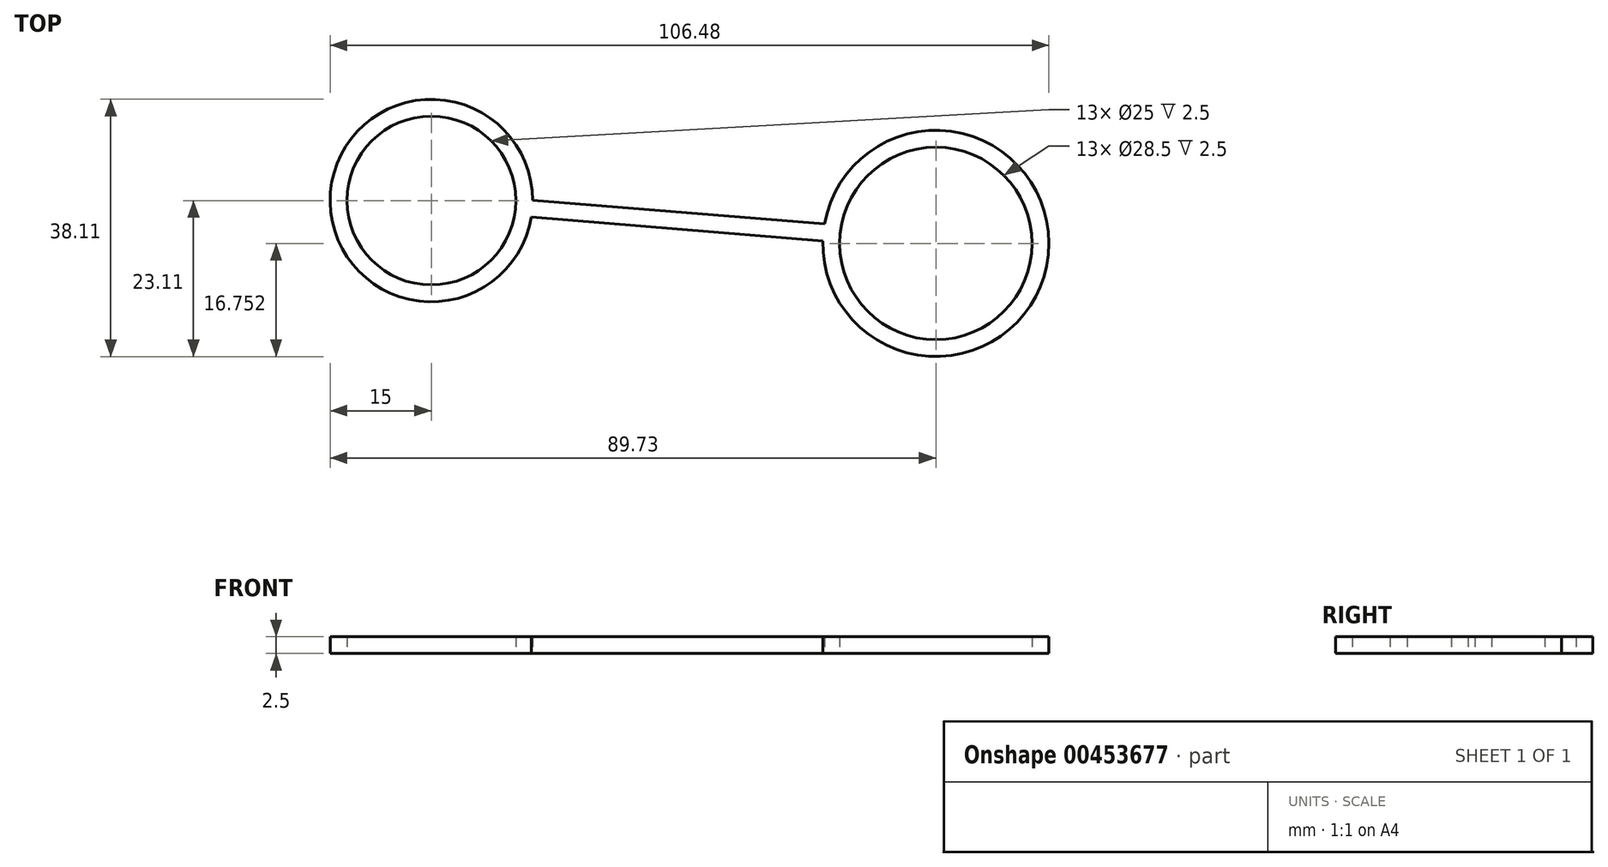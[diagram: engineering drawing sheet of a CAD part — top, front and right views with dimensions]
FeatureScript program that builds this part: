
annotation { "Feature Type Name" : "Feature", "Feature Type Description" : "" }
export const myFeature = defineFeature(function(context is Context, id is Id, definition is map)
    precondition{}
    {
        {
            var Q0;
            Q0=qCreatedBy(makeId("Top.planeOp"),FACE);
            var sketch = newSketch(context, id + "F0", { "sketchPlane" : qUnion([Q0])});
            skArc(sketch, "E0", {"start": v(15, 0.04) * mm, "mid": v(-14.95, 1.21) * mm, "end": v(14.8, -2.46) * mm});
            skCircle(sketch, "E1", {"center": v(0, 0) * mm, "radius": 12.5 * mm});
            skArc(sketch, "E2", {"start": v(57.98, -5.96) * mm, "mid": v(91.4, -8) * mm, "end": v(58.23, -3.47) * mm});
            skCircle(sketch, "E3", {"center": v(74.73, -6.36) * mm, "radius": 14.25 * mm});
            skLineSegment(sketch, "E4", {"start": v(14.8, -2.46) * mm, "end": v(57.98, -5.96) * mm});
            skLineSegment(sketch, "E5", {"start": v(15, 0.04) * mm, "end": v(58.23, -3.47) * mm});
            skSolve(sketch);
        }
        {
            var Q0;
            Q0 = qSketchRegion(id + "F0", true);
            extrude(context, id + "F1", {"entities" : qUnion([Q0]), "depth" : 2.5 * mm});
        }
    });
